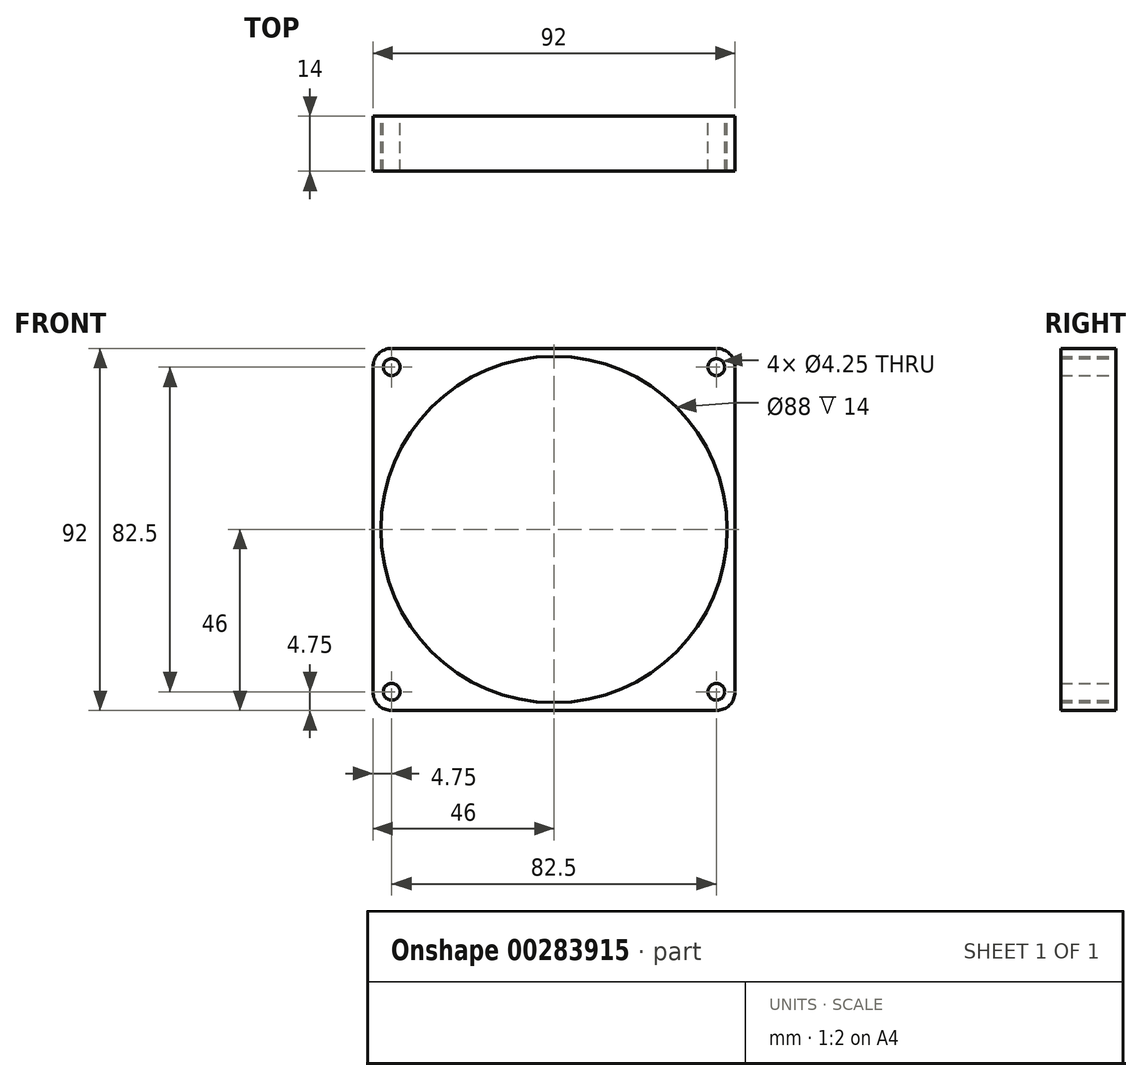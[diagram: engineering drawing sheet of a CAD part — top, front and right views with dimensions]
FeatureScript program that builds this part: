
annotation { "Feature Type Name" : "Feature", "Feature Type Description" : "" }
export const myFeature = defineFeature(function(context is Context, id is Id, definition is map)
    precondition{}
    {
        {
            var Q0;
            Q0=qCreatedBy(makeId("Front.planeOp"),FACE);
            var sketch = newSketch(context, id + "F0", { "sketchPlane" : qUnion([Q0])});
            skLineSegment(sketch, "E0.bottom", {"start": v(46, 46) * mm, "end": v(-46, 46) * mm});
            skLineSegment(sketch, "E0.top", {"start": v(46, -46) * mm, "end": v(-46, -46) * mm});
            skLineSegment(sketch, "E0.left", {"start": v(46, 46) * mm, "end": v(46, -46) * mm});
            skLineSegment(sketch, "E0.right", {"start": v(-46, 46) * mm, "end": v(-46, -46) * mm});
            skPoint(sketch, "E0.middle", {"position": v(0, 0) * mm});
            skCircle(sketch, "E1", {"center": v(0, 0) * mm, "radius": 44 * mm});
            skPoint(sketch, "E2", {"position": v(0, 44) * mm});
            skLineSegment(sketch, "E3", {"start": v(0, 0) * mm, "end": v(-46, 46) * mm, "construction": true});
            skCircle(sketch, "E4", {"center": v(-41.25, 41.25) * mm, "radius": 2.12 * mm});
            skLineSegment(sketch, "E5", {"start": v(0, 0) * mm, "end": v(0, 76.8) * mm, "construction": true});
            skCircle(sketch, "E6.1.0", {"center": v(-41.25, -41.25) * mm, "radius": 2.12 * mm});
            skCircle(sketch, "E6.2.0", {"center": v(41.25, -41.25) * mm, "radius": 2.12 * mm});
            skCircle(sketch, "E6.3.0", {"center": v(41.25, 41.25) * mm, "radius": 2.12 * mm});
            skSolve(sketch);
        }
        {
            var Q0;
            Q0 = qSketchRegion(id + "F0", true);
            extrude(context, id + "F1", {"entities" : qUnion([Q0]), "endBound" : BoundingType.SYMMETRIC, "depth" : 14 * mm});
        }
        {
            var Q0;
            Q0=makeQuery(id+"F1.opExtrude","SWEPT_EDGE",EDGE,{"disambiguationData":[OSD([sQuery(id+"F0.wireOp",EDGE,"E0.bottom"),sQuery(id+"F0.wireOp",EDGE,"E0.right")])]});
            var Q1;
            Q1=makeQuery(id+"F1.opExtrude","SWEPT_EDGE",EDGE,{"disambiguationData":[OSD([sQuery(id+"F0.wireOp",EDGE,"E0.bottom"),sQuery(id+"F0.wireOp",EDGE,"E0.left")])]});
            var Q2;
            Q2=makeQuery(id+"F1.opExtrude","SWEPT_EDGE",EDGE,{"disambiguationData":[OSD([sQuery(id+"F0.wireOp",EDGE,"E0.top"),sQuery(id+"F0.wireOp",EDGE,"E0.left")])]});
            var Q3;
            Q3=makeQuery(id+"F1.opExtrude","SWEPT_EDGE",EDGE,{"disambiguationData":[OSD([sQuery(id+"F0.wireOp",EDGE,"E0.top"),sQuery(id+"F0.wireOp",EDGE,"E0.right")])]});
            fillet(context, id + "F2", {"entities" : qUnion([Q0, Q1, Q2, Q3]), "radius" : 4.75 * mm, "tangentPropagation" : true, "allowEdgeOverflow" : false});
        }
    });
